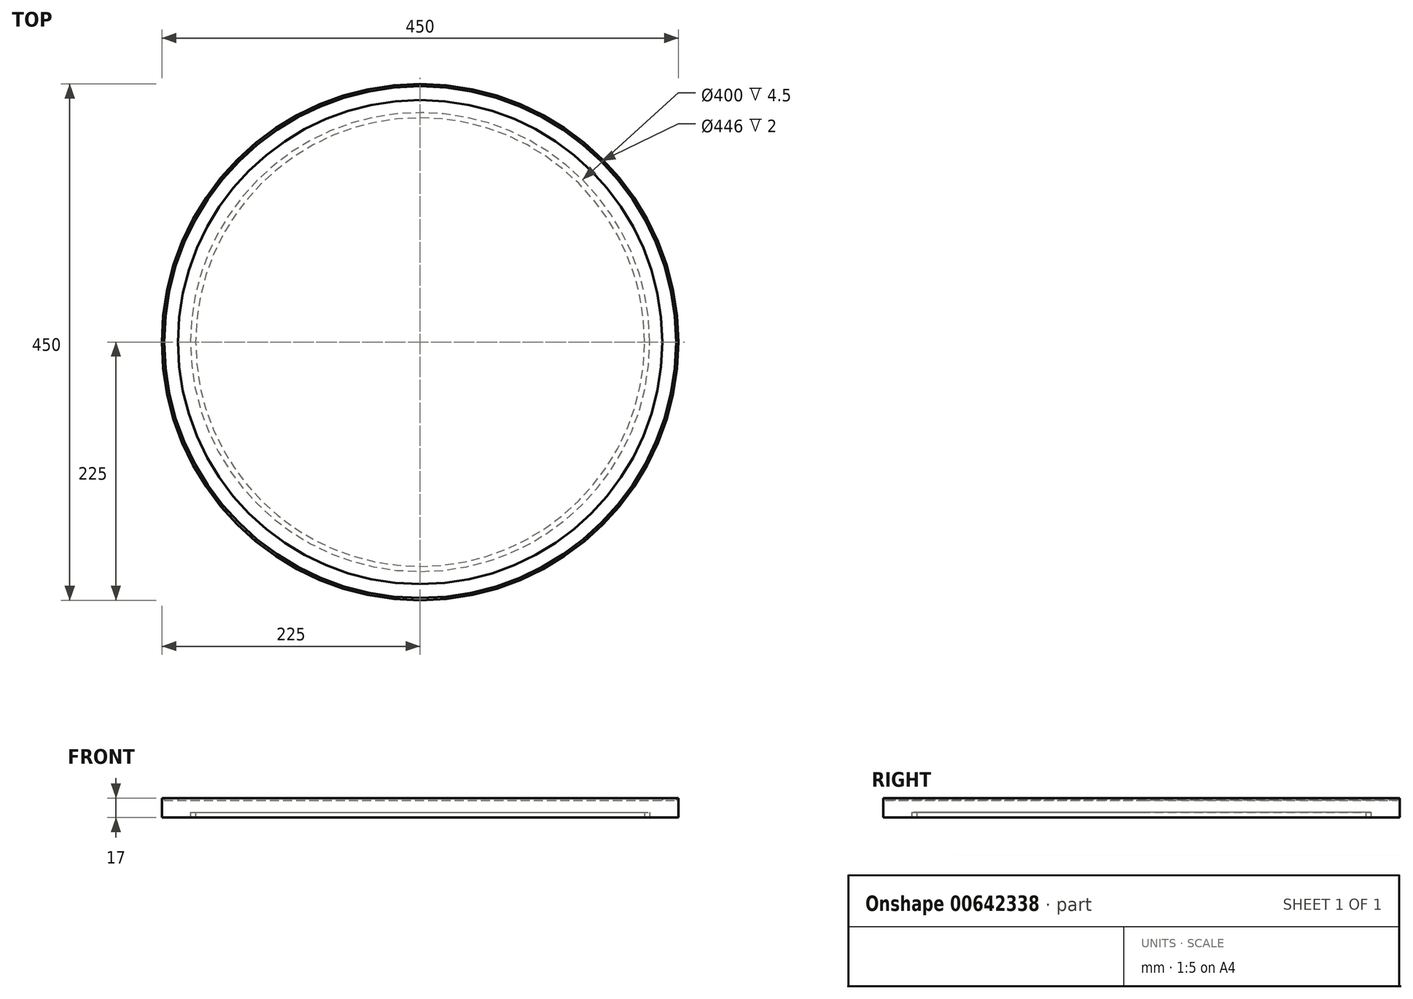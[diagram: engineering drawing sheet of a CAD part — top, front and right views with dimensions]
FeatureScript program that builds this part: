
annotation { "Feature Type Name" : "Feature", "Feature Type Description" : "" }
export const myFeature = defineFeature(function(context is Context, id is Id, definition is map)
    precondition{}
    {
        {
            var Q0;
            Q0=qCreatedBy(makeId("Front.planeOp"),FACE);
            var sketch = newSketch(context, id + "F0", { "sketchPlane" : qUnion([Q0])});
            skLineSegment(sketch, "E0", {"start": v(0, 0) * mm, "end": v(195.5, 0) * mm});
            skLineSegment(sketch, "E1", {"start": v(195.5, 0) * mm, "end": v(195.5, 4.5) * mm});
            skLineSegment(sketch, "E2", {"start": v(195.5, 4.5) * mm, "end": v(200, 4.5) * mm});
            skLineSegment(sketch, "E3", {"start": v(200, 4.5) * mm, "end": v(200, 0) * mm});
            skLineSegment(sketch, "E4", {"start": v(200, 0) * mm, "end": v(225, 0) * mm});
            skLineSegment(sketch, "E5", {"start": v(225, 0) * mm, "end": v(225, 17) * mm});
            skLineSegment(sketch, "E6", {"start": v(225, 17) * mm, "end": v(223, 17) * mm});
            skLineSegment(sketch, "E7", {"start": v(223, 17) * mm, "end": v(223, 15) * mm});
            skLineSegment(sketch, "E8", {"start": v(223, 15) * mm, "end": v(211, 15) * mm});
            skLineSegment(sketch, "E9", {"start": v(211, 15) * mm, "end": v(211, 17) * mm});
            skLineSegment(sketch, "E10", {"start": v(211, 17) * mm, "end": v(0, 17) * mm});
            skLineSegment(sketch, "E11", {"start": v(0, 17) * mm, "end": v(0, 0) * mm});
            skSolve(sketch);
        }
        {
            var Q0;
            Q0=qCreatedBy(makeId("Front.planeOp"),FACE);
            var sketch = newSketch(context, id + "F1", { "sketchPlane" : qUnion([Q0])});
            skLineSegment(sketch, "E12", {"start": v(0, 0) * mm, "end": v(0, 66.87) * mm, "construction": true});
            skSolve(sketch);
        }
        {
            var Q0;
            Q0=makeQuery(id+"F0.imprint","IMPRINT",FACE,{"disambiguationData":[TD([[makeQuery(id+"F0.imprint","IMPRINT",EDGE,{"derivedFrom":sQuery(id+"F0.wireOp",EDGE,"E0")}),1.0]])]});
            var Q1;
            Q1=sQuery(id+"F1.wireOp",EDGE,"E12");
            revolve(context, id + "F2", {"entities" : qUnion([Q0]), "axis" : qUnion([Q1]), "revolveType" : RevolveType.FULL});
        }
    });
